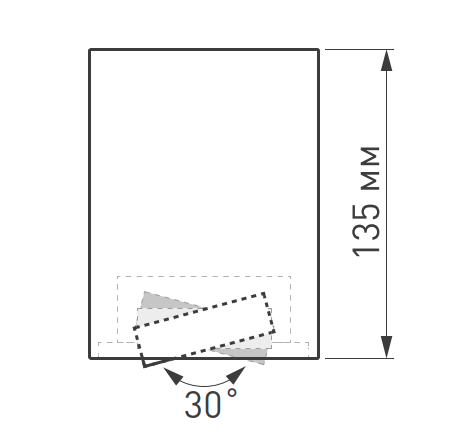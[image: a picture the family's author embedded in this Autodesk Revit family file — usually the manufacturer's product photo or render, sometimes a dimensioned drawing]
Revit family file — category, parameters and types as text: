
# Revit family: CUBUS-S100x100
name_source: partatom
category: Осветительные приборы
revit_build: Autodesk Revit 2017 (Build: 20160225_1515(x64)
units: mm (PartAtom-declared; Revit-internal decimal feet)

## family parameters
Всегда вертикально = Да
Источник света = Да
На основе рабочей плоскости = Нет
Общий = Нет
При загрузке вырезать с полостями = Нет
Размер круглого соединителя = Использовать диаметр
Тип детали = Нормальный
Точка расчета площади = Нет

## types (6) — shared parameters
ADSK_Единица измерения = шт.
ADSK_Завод-изготовитель = ARLIGHT
ADSK_Классификация нагрузок = Освещение
ADSK_Количество фаз = 1
ADSK_Количество фаз числовое = 1
ADSK_Коэффициент мощности = 0.47
ADSK_Масса_Текст = 1.156
ADSK_Наименование = Светильник
ADSK_Напряжение = 230 В
ADSK_Номинальная мощность = 11 Вт
ADSK_Полная мощность = 23 В·А
ADSK_Размер_Высота = 135 мм
ADSK_Размер_Длина = 100 мм
ADSK_Размер_Ширина = 100 мм
ADSK_Ток = 0 А
ARL_Драйвер = Встроенный (DC500mA 14-24V)
ARL_Индекс цветопередачи = >80
ARL_Класс защиты от поражения электрическим током = II
ARL_Класс пылевлагозащиты = IP20
ARL_Область использования = Для освещения и декоративного оформления жилых, офисных и других помещений.
ARL_Рабочая температура окружающей среды = -20...+45 °C
ARL_Серия = CUBUS
ARL_Способ монтажа = Накладной
ARL_Тип товара = Светильник
ARL_Угол обзора = 40°
URL = https://arlight.ru
Видимая форма излучения при визуализации = Нет
Группа модели = Светильники
Изготовитель = ARLIGHT
Изготовитель (сайт) = www.arlight.ru
Изготовитель (телефон) = 8 800 505 26 29
Излучение по диаметру окружности = 45 мм
Полная установленная мощность = 23 В·А
Разработчик = НТЦ Конструктор
Разработчик (URL) = https://constructor.ru
Разработчик (телефон) = +7 (495) 781-05-35
Светофильтр = 16777215
Смещение цветовой температуры при затухании лампы = <Нет>
Угол наклона = 90.00°

## per-type parameters (varying)
| type | ADSK_Код изделия | ADSK_Марка | ARL_Материал корпуса | ARL_Обозначение корпуса | ARL_Цвет покрытия | ARL_Цвет свечения | Комментарии к типоразмеру | Описание | Файл фотометрической сетки |
| 023079 Светильник SP-CUBUS-S100x100WH-11W White 40deg | Арт. 023079 | SP-CUBUS-S100x100WH-11W White 40deg | Металл, белый | Корпус квадратный, металл, цвет белый | Белый | Дневной 5000K | Арт. 023079 | Накладной светильник 11 Вт, белый квадратный корпус. Цвет БЕЛЫЙ 5000K, св.поток 910лм, CRI(Ra)>80, угол 40°, регулируемое направление луча 30°. Размер 100x100x135 мм. Питание AC 220-240V, 11 Вт, драйвер встроенный (DC500mA 14-24V). | 023079 SP-CUBUS-S100x100WH-11W White 40deg.ies |
| 023078 Светильник SP-CUBUS-S100x100WH-11W Day White 40deg | Арт. 023078 | SP-CUBUS-S100x100WH-11W Day White 40deg | Металл, белый | Корпус квадратный, металл, цвет белый | Белый | Дневной 4000K | Арт. 023078 | Накладной светильник 11 Вт, белый квадратный корпус. Цвет ДНЕВНОЙ БЕЛЫЙ 4000K, св.поток 850лм, CRI(Ra)>80, угол 40°, регулируемое направление луча 30°. Размер 100x100x135 мм. Питание AC 220-240V, 11 Вт, драйвер встроенный (DC500mA 14-24V). | 023078 SP-CUBUS-S100x100WH-11W Day White 40deg.ies |
| 020386 Светильник SP-CUBUS-S100x100WH-11W Warm White 40deg | Арт. 020386 | SP-CUBUS-S100x100WH-11W Warm White 40deg | Металл, белый | Корпус квадратный, металл, цвет белый | Белый | Теплый 3000K | Арт. 020386 | Накладной светильник 11 Вт, белый квадратный корпус. ЦветТЕПЛЫЙ БЕЛЫЙ 3000K, св.поток 830лм, CRI(Ra)>80, угол 40°, регулируемое направление луча 30°. Размер 100x100x135 мм. Питание AC 220-240V, 11 Вт, драйвер встроенный (DC500mA 14-24V). | 020386 SP-CUBUS-S100x100WH-11W Warm White 40deg.ies |
| 023081 Светильник SP-CUBUS-S100x100BK-11W Day White 40deg | Арт. 023081 | SP-CUBUS-S100x100BK-11W Day White 40deg | Металл, чёрный | Корпус квадратный, металл, цвет черный | Черный | Дневной 4000K | Арт. 023081 | Накладной светильник 11 Вт, черный квадратный корпус. Цвет ДНЕВНОЙ БЕЛЫЙ 4000K, св.поток 850лм, CRI(Ra)>80, угол 40°, регулируемое направление луча 30°. Размер 100x100x135 мм. Питание AC 220-240V, 11 Вт, драйвер встроенный (DC500mA 14-24V). | 023081 SP-CUBUS-S100x100BK-11W Day White 40deg.ies |
| 023082 Светильник SP-CUBUS-S100x100BK-11W Warm White 40deg | Арт. 023082 | SP-CUBUS-S100x100BK-11W Warm White 40deg | Металл, чёрный | Корпус квадратный, металл, цвет черный | Черный | Теплый 3000K | Арт. 023082 | Накладной светильник 11 Вт, черный квадратный корпус. Цвет ТЕПЛЫЙ БЕЛЫЙ 3000K, св.поток 830 лм, CRI(Ra)>80, угол 40°, регулируемое направление луча 30°. Размер 100x100x135 мм. Питание AC 220-240V, 11 Вт, драйвер встроенный (DC500mA 14-24V). | 023082 SP-CUBUS-S100x100BK-11W Warm White 40deg.ies |
| 023080 Светильник SP-CUBUS-S100x100BK-11W White 40deg | Арт. 023080 | SP-CUBUS-S100x100BK-11W White 40deg | Металл, чёрный | Корпус квадратный, металл, цвет черный | Черный | Дневной 5000K | Арт. 023080 | Накладной светильник 11 Вт, черный квадратный корпус. Цвет БЕЛЫЙ 5000K, св.поток 910лм, CRI(Ra)>80, угол 40°, регулируемое направление луча 30°. Размер 100x100x135 мм. Питание AC 220-240V, 11 Вт, драйвер встроенный (DC500mA 14-24V). | 023080 SP-CUBUS-S100x100BK-11W White 40deg.ies |
